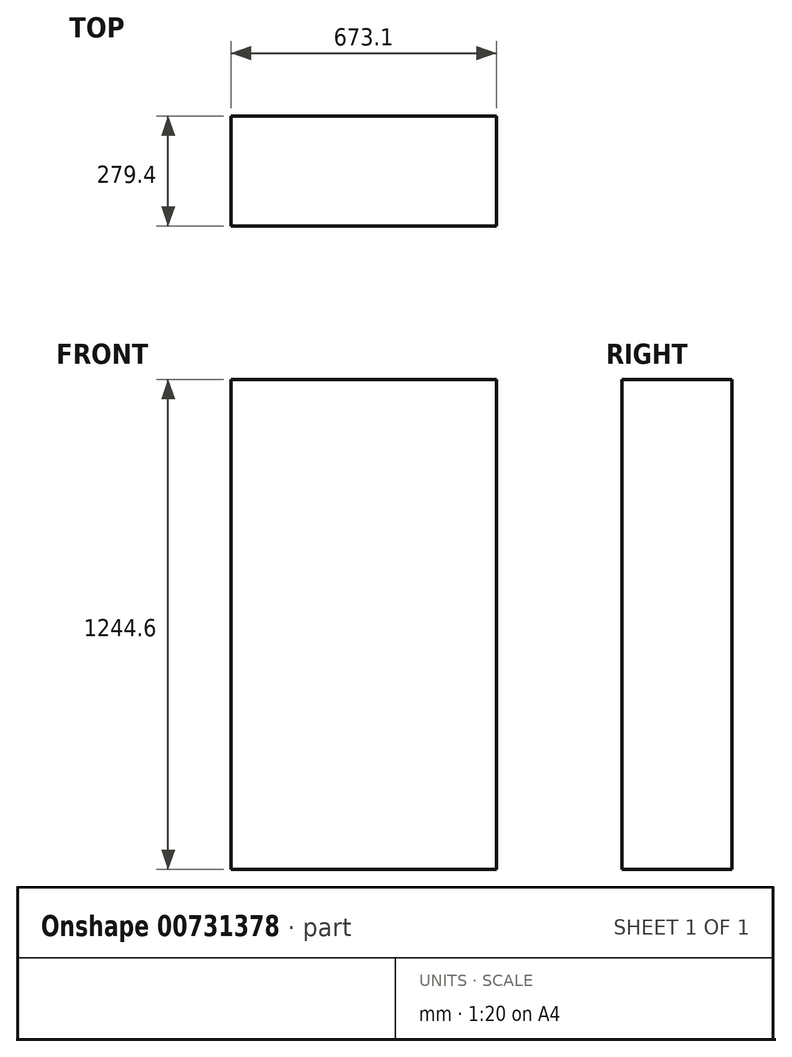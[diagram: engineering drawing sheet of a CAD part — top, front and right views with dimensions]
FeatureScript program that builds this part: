
annotation { "Feature Type Name" : "Feature", "Feature Type Description" : "" }
export const myFeature = defineFeature(function(context is Context, id is Id, definition is map)
    precondition{}
    {
        {
            var Q0;
            Q0=qCreatedBy(makeId("Front.planeOp"),FACE);
            var sketch = newSketch(context, id + "F0", { "sketchPlane" : qUnion([Q0])});
            skLineSegment(sketch, "E0", {"start": v(-332.66, 827.18) * mm, "end": v(340.44, 827.18) * mm});
            skLineSegment(sketch, "E1", {"start": v(-332.66, 827.18) * mm, "end": v(-332.66, -417.42) * mm});
            skLineSegment(sketch, "E2", {"start": v(340.44, 827.18) * mm, "end": v(340.44, -417.42) * mm});
            skLineSegment(sketch, "E3", {"start": v(340.44, -417.42) * mm, "end": v(-332.66, -417.42) * mm});
            skSolve(sketch);
        }
        {
            var Q0;
            Q0=makeQuery(id+"F0.imprint","IMPRINT",FACE,{"disambiguationData":[TD([[makeQuery(id+"F0.imprint","IMPRINT",EDGE,{"derivedFrom":sQuery(id+"F0.wireOp",EDGE,"E0")}),-1.0]])]});
            extrude(context, id + "F1", {"entities" : qUnion([Q0]), "depth" : 279.4 * mm, "offsetDistance" : 25.4 * mm});
        }
    });
